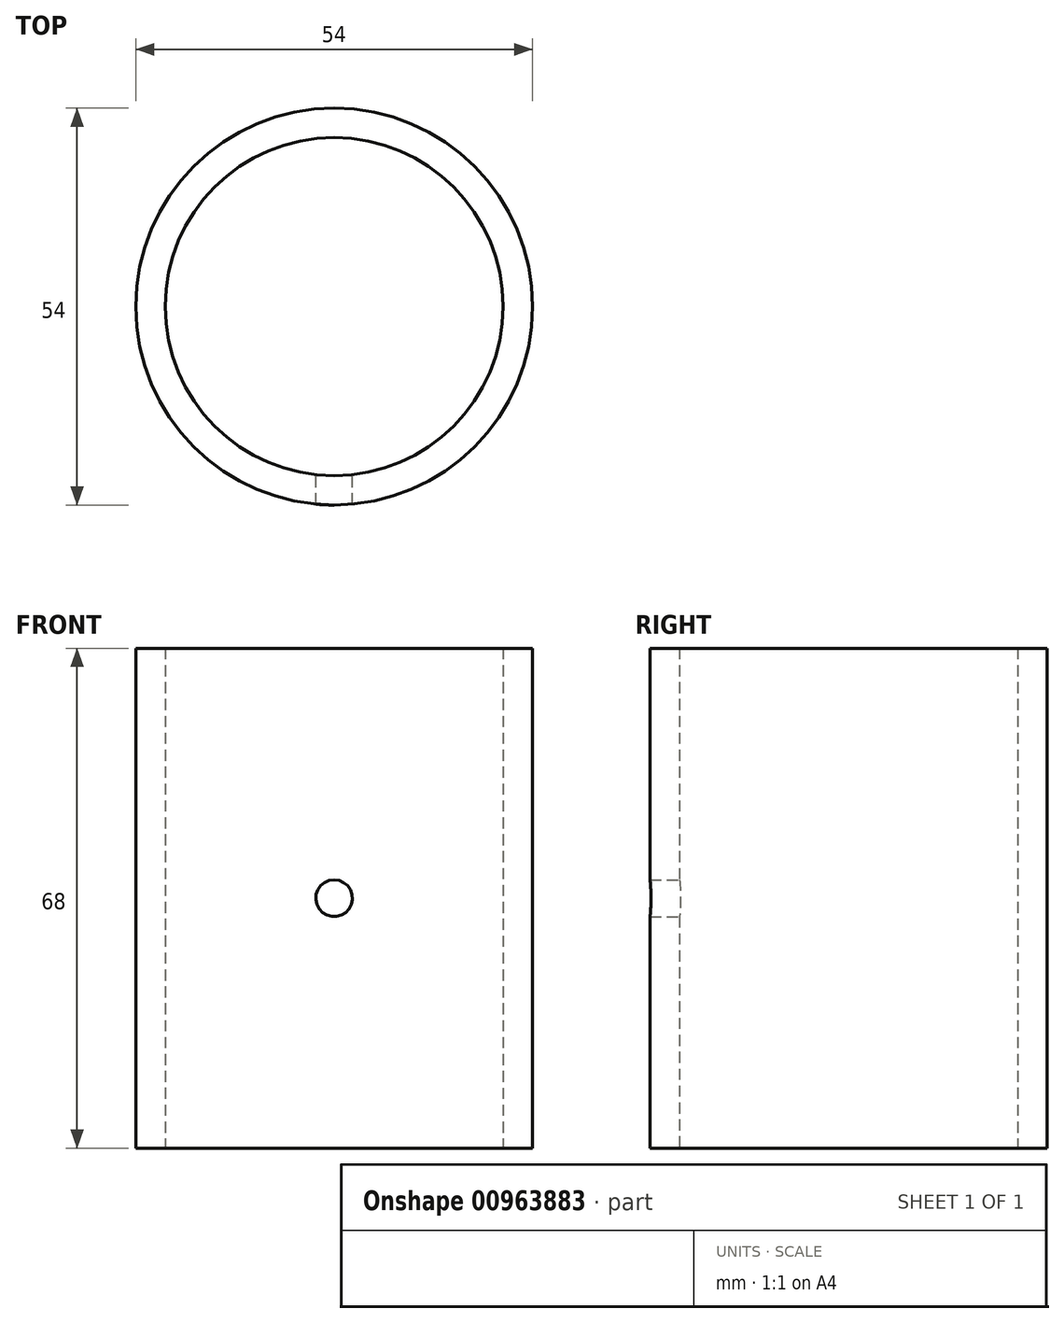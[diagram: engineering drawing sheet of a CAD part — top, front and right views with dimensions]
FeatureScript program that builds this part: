
annotation { "Feature Type Name" : "Feature", "Feature Type Description" : "" }
export const myFeature = defineFeature(function(context is Context, id is Id, definition is map)
    precondition{}
    {
        {
            var Q0;
            Q0=qCreatedBy(makeId("Top.planeOp"),FACE);
            var sketch = newSketch(context, id + "F0", { "sketchPlane" : qUnion([Q0])});
            skCircle(sketch, "E0", {"center": v(0, 0) * mm, "radius": 23 * mm});
            skCircle(sketch, "E1", {"center": v(0, 0) * mm, "radius": 27 * mm});
            skSolve(sketch);
        }
        {
            var Q0;
            Q0=makeQuery(id+"F0.imprint","IMPRINT",FACE,{"disambiguationData":[TD([[makeQuery(id+"F0.imprint","IMPRINT",EDGE,{"derivedFrom":sQuery(id+"F0.wireOp",EDGE,"E0")}),-1.0]])]});
            extrude(context, id + "F1", {"entities" : qUnion([Q0]), "depth" : 68 * mm, "offsetDistance" : 25 * mm});
        }
        {
            var Q0;
            Q0=makeQuery(id+"F1.opExtrude","CAP_FACE",FACE,{"disambiguationData":[OSD([sQuery(id+"F0.wireOp",EDGE,"E0"),sQuery(id+"F0.wireOp",EDGE,"E1")])],"isStart":false});
            var sketch = newSketch(context, id + "F2", { "sketchPlane" : qUnion([Q0])});
            skLineSegment(sketch, "E2", {"start": v(-36.8, 0) * mm, "end": v(50.33, 0) * mm, "construction": true});
            skSolve(sketch);
        }
        {
            var Q0;
            Q0=qCreatedBy(makeId("Front.planeOp"),FACE);
            var sketch = newSketch(context, id + "F3", { "sketchPlane" : qUnion([Q0])});
            skLineSegment(sketch, "E3", {"start": v(0, 0) * mm, "end": v(0, 68) * mm, "construction": true});
            skCircle(sketch, "E4", {"center": v(0, 34) * mm, "radius": 2.5 * mm});
            skSolve(sketch);
        }
        {
            var Q0;
            Q0=makeQuery(id+"F3.imprint","IMPRINT",FACE,{"disambiguationData":[TD([[makeQuery(id+"F3.imprint","IMPRINT",EDGE,{"derivedFrom":sQuery(id+"F3.wireOp",EDGE,"E4")}),1.0]])]});
            extrude(context, id + "F4", {"entities" : qUnion([Q0]), "operationType" : NewBodyOperationType.REMOVE, "endBound" : BoundingType.THROUGH_ALL, "depth" : 25 * mm, "offsetDistance" : 25 * mm});
        }
    });
